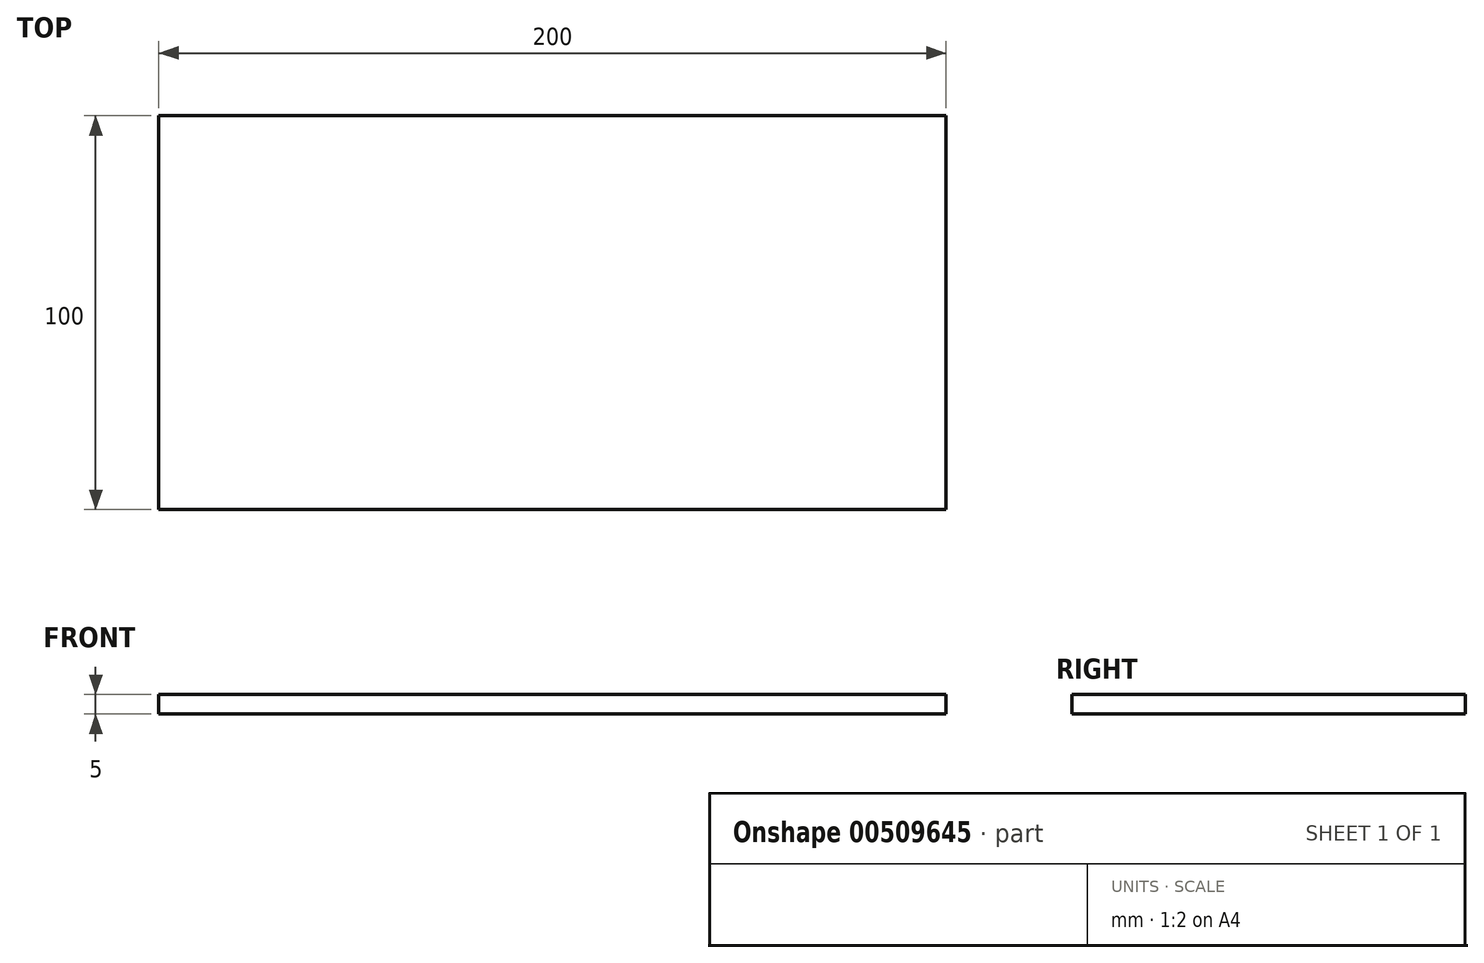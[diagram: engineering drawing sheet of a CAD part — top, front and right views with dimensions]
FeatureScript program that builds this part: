
annotation { "Feature Type Name" : "Feature", "Feature Type Description" : "" }
export const myFeature = defineFeature(function(context is Context, id is Id, definition is map)
    precondition{}
    {
        {
            var Q0;
            Q0=qCreatedBy(makeId("Front.planeOp"),FACE);
            var sketch = newSketch(context, id + "F0", { "sketchPlane" : qUnion([Q0])});
            skLineSegment(sketch, "E0.bottom", {"start": v(-139.22, 26.26) * mm, "end": v(60.78, 26.26) * mm});
            skLineSegment(sketch, "E0.top", {"start": v(-139.22, 21.26) * mm, "end": v(60.78, 21.26) * mm});
            skLineSegment(sketch, "E0.left", {"start": v(-139.22, 26.26) * mm, "end": v(-139.22, 21.26) * mm});
            skLineSegment(sketch, "E0.right", {"start": v(60.78, 26.26) * mm, "end": v(60.78, 21.26) * mm});
            skSolve(sketch);
        }
        {
            var Q0;
            Q0 = qSketchRegion(id + "F0", true);
            extrude(context, id + "F1", {"entities" : qUnion([Q0]), "depth" : 100 * mm, "offsetDistance" : 25 * mm});
        }
    });
